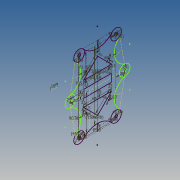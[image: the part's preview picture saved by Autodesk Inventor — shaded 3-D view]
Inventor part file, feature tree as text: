
AUTODESK INVENTOR PART (.ipt)
format: ipt  version: 2014 (Build 180170000, 170)  size: 135,168 bytes
history: native  units: mm
features: sketch x1
ambient origin geometry x8: Origin, YZ Plane, XZ Plane, XY Plane, X Axis, Y Axis, Z Axis, Center Point
feature tree (1):
  sketch  "Sketch1"  dims[d0=165.0mm d1=85.5mm d2=82.5mm d3=20.0mm d4=20.0mm d5=25.0mm d6=25.0mm d7=25.0mm d8=25.0mm d9=25.0mm d10=25.0mm d11=7.0mm d12=7.0mm d13=7.0mm d14=7.0mm d15=7.0mm d16=7.0mm d17=45.0deg d18=45.0deg d19=45.0deg d20=45.0deg d21=45.0deg d22=45.0deg d23=45.0deg d24=18.0mm d25=90.0deg d26=16.0mm d27=16.0mm d28=11.0mm d29=11.0mm d30=150.67767mm d31=61.6967mm d32=63.5mm d33=18.0mm d34=73.282503mm d35=31.0mm d36=46.0mm d37=46.0mm d38=65.053824mm d39=18.0mm d40=65.0mm d41=46.0mm d42=46.0mm d43=18.0mm d44=2.0mm d45=6.5mm d46=2.0mm d47=2.0mm d48=33.0mm d49=17.0mm d50=17.0mm d51=33.0mm d52=2.0mm d53=2.0mm d54=33.0mm d55=33.0mm d56=17.0mm d57=17.0mm]
